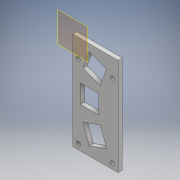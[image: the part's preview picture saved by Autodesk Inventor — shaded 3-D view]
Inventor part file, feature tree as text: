
AUTODESK INVENTOR PART (.ipt)
format: ipt  version: 2017 (Build 210142000, 142)  size: 141,824 bytes
history: native  units: mm
features: other x3, plane x1, extrude x1, sketch x1
ambient origin geometry x8: Origin, YZ Plane, XZ Plane, XY Plane, X Axis, Y Axis, Z Axis, Center Point
bodies: Solid3 (feature_tree)
feature tree (6):
  other  "k2_t2_base.ipt"
  plane  "Work Plane1"
  extrude  "Extrusion3"  Depth=10.0mm
  sketch  "Sketch3"  dims[d50=10.0mm d51=0.0mm d52=10.0mm d67=13.5mm d68=13.5mm d69=55.0mm d70=20.0mm d72=3.490659mm d74=20.0mm d76=3.490659mm d78=5.5mm d79=5.0mm]
  other  "Solid1::k2_t2_base.ipt"
  other  "TaggingFeature2"
